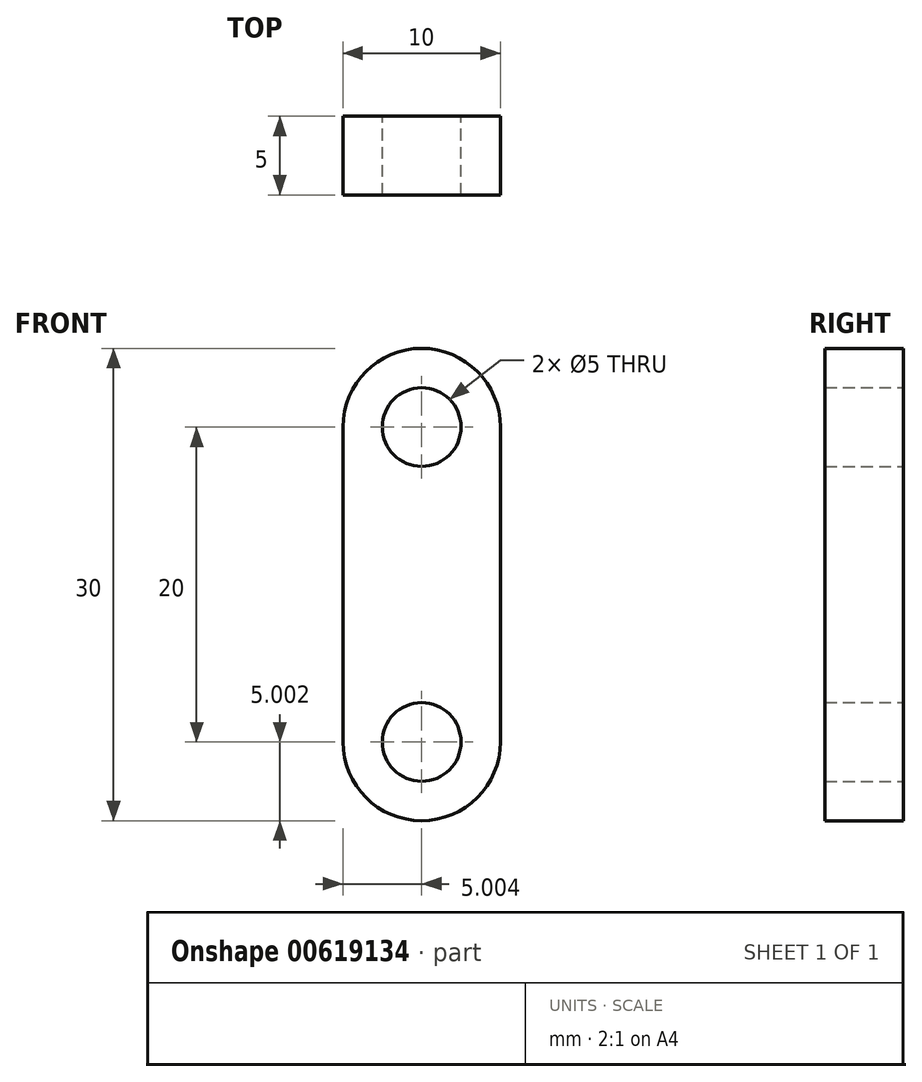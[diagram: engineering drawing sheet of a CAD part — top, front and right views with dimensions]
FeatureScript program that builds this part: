
annotation { "Feature Type Name" : "Feature", "Feature Type Description" : "" }
export const myFeature = defineFeature(function(context is Context, id is Id, definition is map)
    precondition{}
    {
        {
            var Q0;
            Q0=qCreatedBy(makeId("Front.planeOp"),FACE);
            var sketch = newSketch(context, id + "F0", { "sketchPlane" : qUnion([Q0])});
            skLineSegment(sketch, "E0", {"start": v(-45.19, 3.38) * mm, "end": v(-45.19, -16.62) * mm});
            skArc(sketch, "E1", {"start": v(-45.19, -16.62) * mm, "mid": v(-40.19, -21.62) * mm, "end": v(-35.19, -16.62) * mm});
            skLineSegment(sketch, "E2", {"start": v(-35.19, -16.62) * mm, "end": v(-35.19, 3.38) * mm});
            skArc(sketch, "E3", {"start": v(-35.19, 3.38) * mm, "mid": v(-40.19, 8.38) * mm, "end": v(-45.19, 3.38) * mm});
            skCircle(sketch, "E4", {"center": v(-40.19, 3.38) * mm, "radius": 2.5 * mm});
            skCircle(sketch, "E5", {"center": v(-40.19, -16.62) * mm, "radius": 2.5 * mm});
            skSolve(sketch);
        }
        {
            var Q0;
            Q0 = qSketchRegion(id + "F0", true);
            extrude(context, id + "F1", {"entities" : qUnion([Q0]), "depth" : 5 * mm, "offsetDistance" : 25 * mm});
        }
    });
